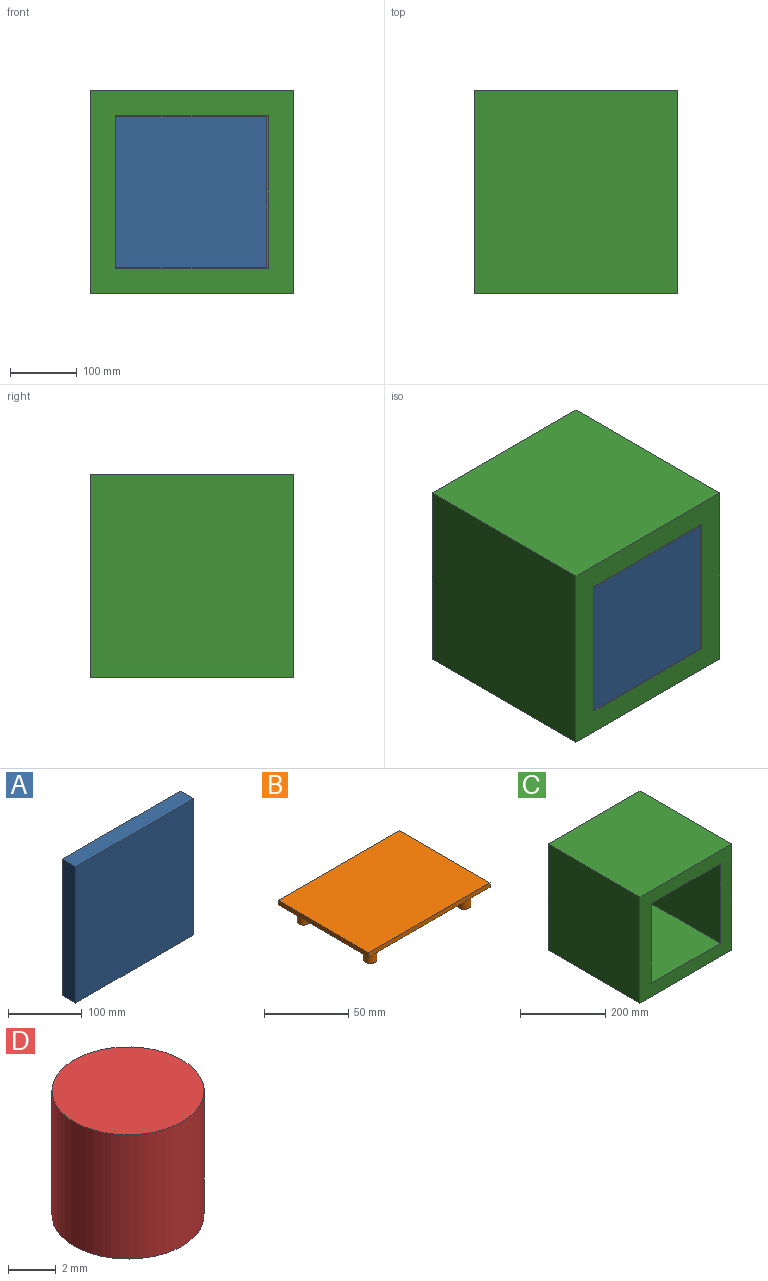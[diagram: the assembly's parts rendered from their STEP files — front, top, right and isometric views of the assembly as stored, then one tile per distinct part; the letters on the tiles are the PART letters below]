
ASSEMBLY  parts=4 mates=4
PART A: 6 faces, bbox 226.1x25.4x226.1 mm
  f0: plane 226.06x25.4mm, normal (0,0,1), area 5741.9mm2, adj f1,f3,f4,f5
  f1: plane 226.06x25.4mm, normal (-1,0,0), area 5741.9mm2, adj f0,f2,f4,f5
  f2: plane 226.06x25.4mm, normal (0,0,-1), area 5741.9mm2, adj f1,f3,f4,f5
  f3: plane 226.06x25.4mm, normal (1,0,0), area 5741.9mm2, adj f0,f2,f4,f5
  f4: plane 226.06x226.06mm, normal (0,-1,0), area 51103.1mm2, adj f0,f1,f2,f3
  f5: plane 226.06x226.06mm, normal (0,1,0), area 51103.1mm2, adj f0,f1,f2,f3
PART B: 14 faces, bbox 101.6x76.2x15.9 mm
  f0: plane 101.6x3.18mm, normal (0,1,0), area 322.6mm2, adj f1,f3,f4,f5
  f1: plane 76.2x3.18mm, normal (-1,0,0), area 241.9mm2, adj f0,f2,f4,f5
  f2: plane 101.6x3.18mm, normal (0,-1,0), area 322.6mm2, adj f1,f3,f4,f5
  f3: plane 76.2x3.18mm, normal (1,0,0), area 241.9mm2, adj f0,f2,f4,f5
  f4: plane 101.6x76.2mm, normal (0,0,1), area 7741.9mm2, adj f0,f1,f2,f3
  f5: plane 101.6x76.2mm, normal (0,0,-1), area 7559.5mm2, adj f0,f1,f2,f3,f6,f8,f10,f12
  f6: cylinder r=3.81mm len=12.7mm, axis (0,0,1), area 304mm2, adj f5,f7
  f7: plane 7.62x7.62mm, normal (0,0,-1), area 45.6mm2, adj f6
  f8: cylinder r=3.81mm len=12.7mm, axis (0,0,1), area 304mm2, adj f5,f9
  f9: plane 7.62x7.62mm, normal (0,0,-1), area 45.6mm2, adj f8
  f10: cylinder r=3.81mm len=12.7mm, axis (0,0,1), area 304mm2, adj f5,f11
  f11: plane 7.62x7.62mm, normal (0,0,-1), area 45.6mm2, adj f10
  f12: cylinder r=3.81mm len=12.7mm, axis (0,0,1), area 304mm2, adj f5,f13
  f13: plane 7.62x7.62mm, normal (0,0,-1), area 45.6mm2, adj f12
PART C: 11 faces, bbox 304.8x304.8x304.8 mm
  f0: plane 304.8x304.8mm, normal (0,-1,0), area 40645.1mm2, adj f1,f2,f3,f4,f6,f7,f8,f9
  f1: plane 304.8x304.8mm, normal (0,0,1), area 92903mm2, adj f0,f2,f4,f5
  f2: plane 304.8x304.8mm, normal (-1,0,0), area 92903mm2, adj f0,f1,f3,f5
  f3: plane 304.8x304.8mm, normal (0,0,-1), area 92903mm2, adj f0,f2,f4,f5
  f4: plane 304.8x304.8mm, normal (1,0,0), area 92903mm2, adj f0,f1,f3,f5
  f5: plane 304.8x304.8mm, normal (0,1,0), area 92903mm2, adj f1,f2,f3,f4
  f6: plane 254x228.6mm, normal (0,0,-1), area 58064.4mm2, adj f0,f7,f9,f10
  f7: plane 254x228.6mm, normal (1,0,0), area 58064.4mm2, adj f0,f6,f8,f10
  f8: plane 254x228.6mm, normal (0,0,1), area 58064.4mm2, adj f0,f7,f9,f10
  f9: plane 254x228.6mm, normal (-1,0,0), area 58064.4mm2, adj f0,f6,f8,f10
  f10: plane 228.6x228.6mm, normal (0,-1,0), area 52258mm2, adj f6,f7,f8,f9
PART D: 3 faces, bbox 6.4x6.4x6.4 mm
  f0: cylinder r=3.17mm len=6.35mm, axis (0,0,-1), area 126.7mm2, adj f1,f2
  f1: plane 6.35x6.35mm, normal (0,0,1), area 31.7mm2, adj f0
  f2: plane 6.35x6.35mm, normal (0,0,-1), area 31.7mm2, adj f0
PLACE A t=(20.69,-65.21,24.63)mm
PLACE B t=(13.08,35.31,-77.08)mm
PLACE C t=(21.96,74.49,24.52)mm
PLACE D t=(13.08,35.31,-73.91)mm
MATE planar D.f0 <-> B.f4  axis (0,0,-1) through (13.08,35.31,-73.91)mm
MATE planar A.f1 <-> C.f7  axis (-1,0,0) through (-92.34,-65.21,24.63)mm
MATE planar A.f4 <-> C.f0  axis (0,-1,0) through (20.69,-77.91,24.63)mm
MATE planar B.f6 <-> C.f8  axis (0,0,-1) through (-26.29,7.37,-89.78)mm
